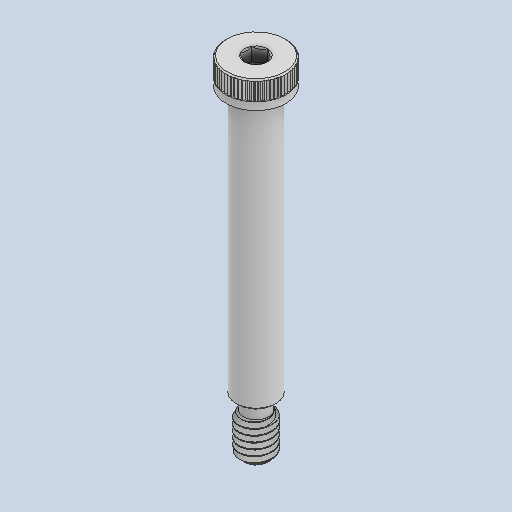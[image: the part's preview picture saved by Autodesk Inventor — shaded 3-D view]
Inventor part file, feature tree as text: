
AUTODESK INVENTOR PART (.ipt)
format: ipt  version: 2022.3 (Build 263350000, 350)  size: 442,880 bytes
history: native  units: in
note: dims shown in document units (in); Inventor stores cm internally (conversion verified against a paired STEP export)
features: chamfer x1
ambient origin geometry x8: Origin, YZ Plane, XZ Plane, XY Plane, X Axis, Y Axis, Z Axis, Center Point
bodies: Solid1 (feature_tree)
feature tree (1):
  chamfer  "Chamfer3"  [1 undecoded]
note: 1 required parameter value undecoded (feature->parameter linkage not recoverable at this tier; creation-order binding heuristic only, values carry confidence <= 0.55)
